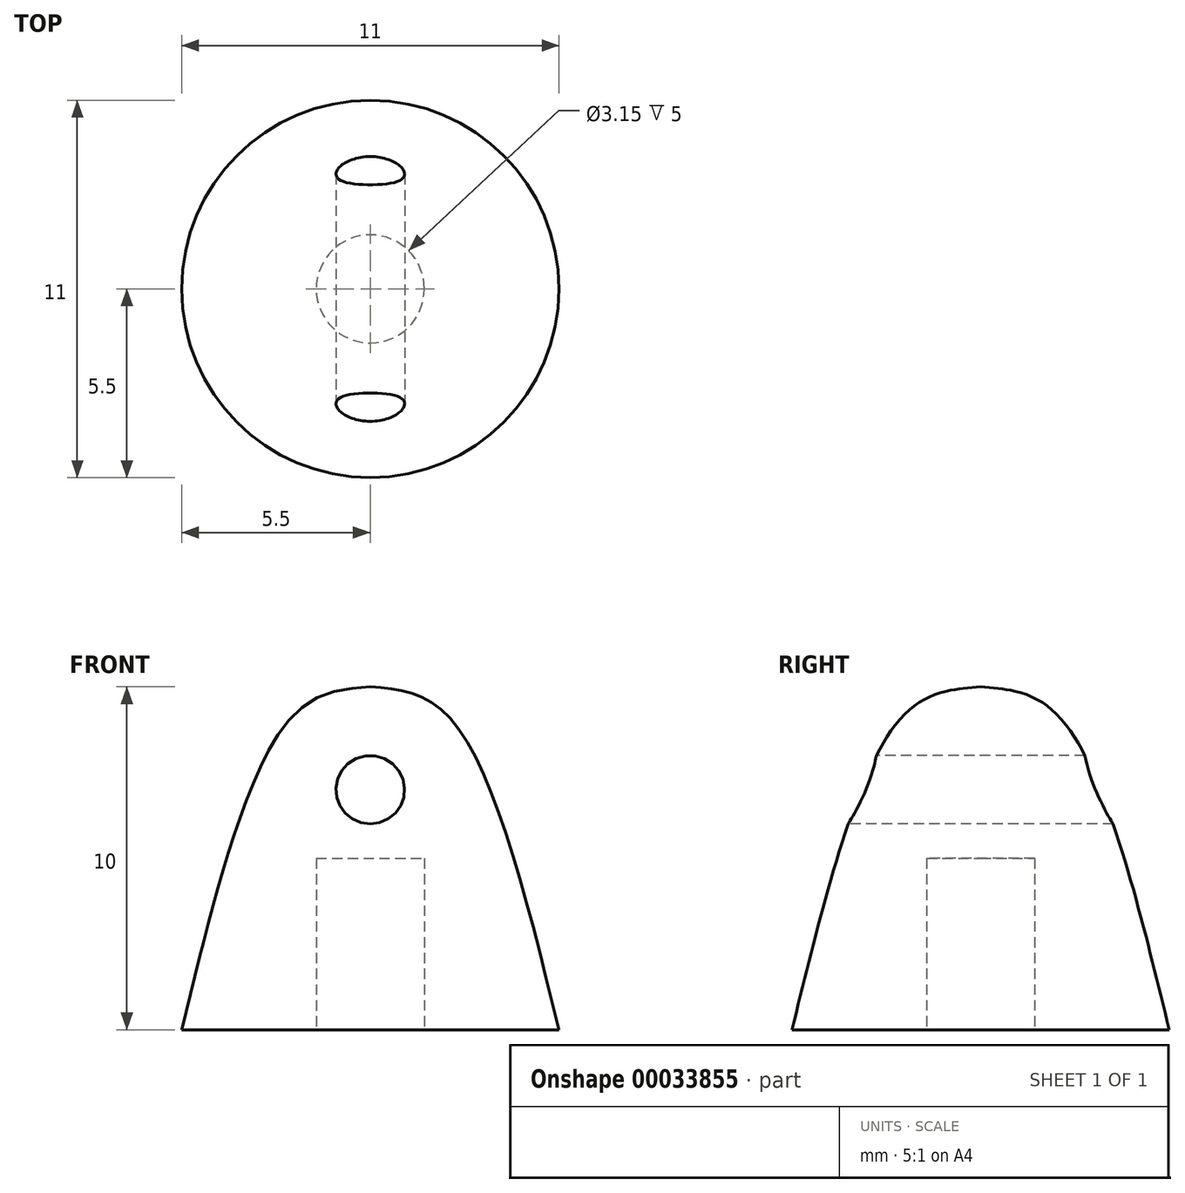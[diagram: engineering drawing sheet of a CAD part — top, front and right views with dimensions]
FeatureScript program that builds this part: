
annotation { "Feature Type Name" : "Feature", "Feature Type Description" : "" }
export const myFeature = defineFeature(function(context is Context, id is Id, definition is map)
    precondition{}
    {
        {
            var Q0;
            Q0=qCreatedBy(makeId("Front.planeOp"),FACE);
            var sketch = newSketch(context, id + "F0", { "sketchPlane" : qUnion([Q0])});
            skLineSegment(sketch, "E0.bottom", {"start": v(1.57, 0) * mm, "end": v(5.5, 0) * mm});
            skLineSegment(sketch, "E0.left", {"start": v(0, 5) * mm, "end": v(0, 10) * mm});
            skFitSpline(sketch, "E1", {"points": [v(0, 10) * mm, v(2.21, 9.2) * mm, v(5.5, 0) * mm], "startDerivative": vector(7.02, -0.55) * mm, "endDerivative": vector(4.3, -17.51) * mm});
            skLineSegment(sketch, "E2.top", {"start": v(0, 5) * mm, "end": v(1.57, 5) * mm});
            skLineSegment(sketch, "E2.right", {"start": v(1.57, 0) * mm, "end": v(1.57, 5) * mm});
            skSolve(sketch);
        }
        {
            var Q0;
            Q0=makeQuery(id+"F0.imprint","IMPRINT",FACE,{"disambiguationData":[TD([[makeQuery(id+"F0.imprint","IMPRINT",EDGE,{"derivedFrom":sQuery(id+"F0.wireOp",EDGE,"E0.bottom")}),1.0]])]});
            var Q1;
            Q1=sQuery(id+"F0.wireOp",EDGE,"E0.left");
            revolve(context, id + "F1", {"entities" : qUnion([Q0]), "axis" : qUnion([Q1]), "revolveType" : RevolveType.FULL});
        }
        {
            var Q0;
            Q0=qCreatedBy(makeId("Front.planeOp"),FACE);
            var sketch = newSketch(context, id + "F2", { "sketchPlane" : qUnion([Q0])});
            skCircle(sketch, "E3", {"center": v(0, 7) * mm, "radius": 1 * mm});
            skSolve(sketch);
        }
        {
            var Q0;
            Q0=qSketchRegion(id+"F2",true);
            extrude(context, id + "F3", {"entities" : qUnion([Q0]), "operationType" : NewBodyOperationType.REMOVE, "endBound" : BoundingType.SYMMETRIC, "oppositeDirection" : true, "depth" : 10 * mm});
        }
    });
